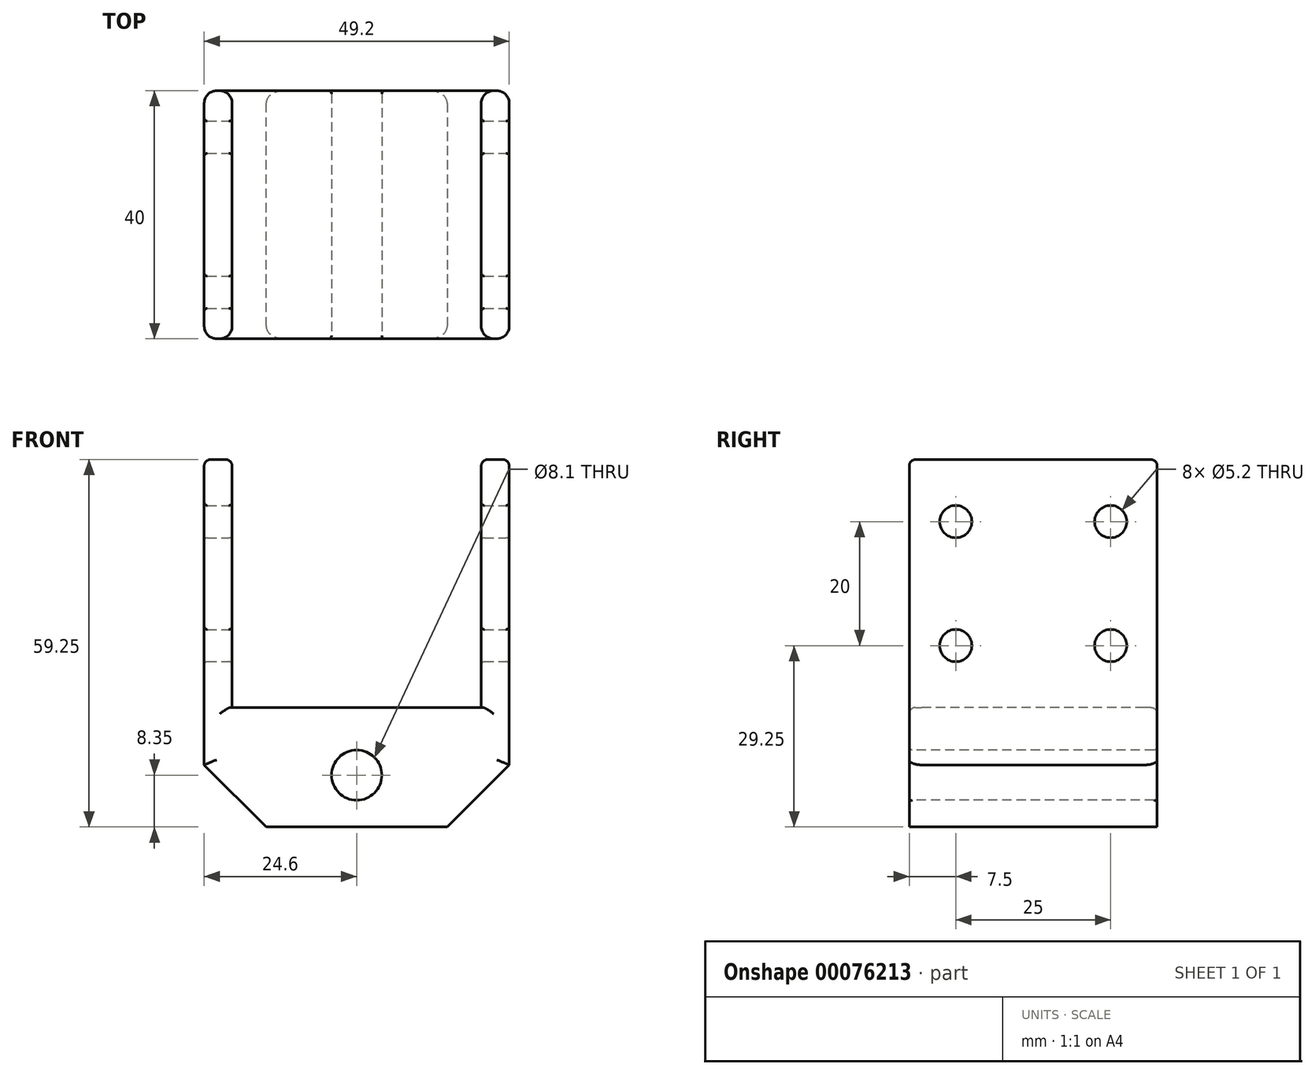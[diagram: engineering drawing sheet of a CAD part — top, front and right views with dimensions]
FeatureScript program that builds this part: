
annotation { "Feature Type Name" : "Feature", "Feature Type Description" : "" }
export const myFeature = defineFeature(function(context is Context, id is Id, definition is map)
    precondition{}
    {
        {
            assignVariable(context, id + "F0", {"name" : "HolderW", "anyValue" : 4.5});
        }
        {
            assignVariable(context, id + "F1", {"name" : "PlateH", "anyValue" : 6.75});
        }
        {
            assignVariable(context, id + "F2", {"name" : "RodD", "anyValue" : 8});
        }
        {
            assignVariable(context, id + "F3", {"name" : "ExtrusionH", "anyValue" : 40});
        }
        {
            var Q0;
            Q0=qCreatedBy(makeId("Top.planeOp"),FACE);
            var sketch = newSketch(context, id + "F4", { "sketchPlane" : qUnion([Q0])});
            skLineSegment(sketch, "E0.bottom", {"start": v(-24.6, 20) * mm, "end": v(24.6, 20) * mm});
            skLineSegment(sketch, "E0.top", {"start": v(-24.6, -20) * mm, "end": v(24.6, -20) * mm});
            skLineSegment(sketch, "E0.left", {"start": v(-24.6, 20) * mm, "end": v(-24.6, -20) * mm});
            skLineSegment(sketch, "E0.right", {"start": v(24.6, 20) * mm, "end": v(24.6, -20) * mm});
            skLineSegment(sketch, "E1", {"start": v(-20.1, 20) * mm, "end": v(-20.1, -20) * mm, "construction": true});
            skLineSegment(sketch, "E2", {"start": v(20.1, 20) * mm, "end": v(20.1, -20) * mm, "construction": true});
            skSolve(sketch);
        }
        {
            var Q0;
            Q0 = qSketchRegion(id + "F4", true);
            extrude(context, id + "F5", {"entities" : qUnion([Q0]), "depth" : (getVariable(context, 'HolderW') + getVariable(context, 'RodD') + getVariable(context, 'PlateH')) * mm});
        }
        {
            var Q0;
            Q0=makeQuery(id+"F5.opExtrude","CAP_FACE",FACE,{"disambiguationData":[OSD([sQuery(id+"F4.wireOp",EDGE,"E0.bottom"),sQuery(id+"F4.wireOp",EDGE,"E0.top"),sQuery(id+"F4.wireOp",EDGE,"E0.left"),sQuery(id+"F4.wireOp",EDGE,"E0.right")])],"isStart":false});
            var sketch = newSketch(context, id + "F6", { "sketchPlane" : qUnion([Q0])});
            skLineSegment(sketch, "E3", {"start": v(-20.1, 20) * mm, "end": v(-20.1, -20) * mm});
            skLineSegment(sketch, "E4", {"start": v(20.1, 20) * mm, "end": v(20.1, -20) * mm});
            skSolve(sketch);
        }
        {
            var Q0;
            {var subQ0=sQuery(id+"F6.wireOp",EDGE,"E3");Q0=makeQuery(id+"F6.imprint","IMPRINT",FACE,{"disambiguationData":[TD([[makeQuery(id+"F6.imprint","IMPRINT",EDGE,{"derivedFrom":subQ0}),-1.0]])]});}
            var Q1;
            {var subQ0=sQuery(id+"F6.wireOp",EDGE,"E4");Q1=makeQuery(id+"F6.imprint","IMPRINT",FACE,{"disambiguationData":[TD([[makeQuery(id+"F6.imprint","IMPRINT",EDGE,{"derivedFrom":subQ0}),1.0]])]});}
            extrude(context, id + "F7", {"entities" : qUnion([Q0, Q1]), "operationType" : NewBodyOperationType.ADD, "depth" : (getVariable(context, 'ExtrusionH')) * mm});
        }
        {
            var Q0;
            {var subQ0=sQuery(id+"F4.wireOp",EDGE,"E0.top");var subQ1=makeQuery(id+"F5.opExtrude","CAP_EDGE",EDGE,{"disambiguationData":[OSD([subQ0])],"isStart":false});Q0=makeQuery(id+"F7.boolean.opBoolean","MERGE",FACE,{"derivedFrom":[makeQuery(id+"F5.opExtrude","SWEPT_FACE",FACE,{"disambiguationData":[OSD([subQ0])]}),makeQuery(id+"F7.opExtrude","SWEPT_FACE",FACE,{"disambiguationData":[OSD([subQ0]),TDD([makeQuery(id+"F6.imprint","IMPRINT",EDGE,{"disambiguationData":[TD([[makeQuery(id+"F6.imprint","INTERSECT",VERTEX,{"derivedFrom":[subQ1,makeQuery(id+"F5.opExtrude","CAP_EDGE",EDGE,{"disambiguationData":[OSD([sQuery(id+"F4.wireOp",EDGE,"E0.left")])],"isStart":false})]}),-1.0]])],"derivedFrom":subQ1})])]}),makeQuery(id+"F7.opExtrude","SWEPT_FACE",FACE,{"disambiguationData":[OSD([subQ0]),TDD([makeQuery(id+"F6.imprint","IMPRINT",EDGE,{"disambiguationData":[TD([[makeQuery(id+"F6.imprint","INTERSECT",VERTEX,{"derivedFrom":[subQ1,makeQuery(id+"F5.opExtrude","CAP_EDGE",EDGE,{"disambiguationData":[OSD([sQuery(id+"F4.wireOp",EDGE,"E0.right")])],"isStart":false})]}),1.0]])],"derivedFrom":subQ1})])]})]});}
            var sketch = newSketch(context, id + "F8", { "sketchPlane" : qUnion([Q0])});
            skCircle(sketch, "E5", {"center": v(0, 8.35) * mm, "radius": 4.05 * mm});
            skSolve(sketch);
        }
        {
            var Q0;
            Q0=makeQuery(id+"F8.imprint","IMPRINT",FACE,{"disambiguationData":[TD([[makeQuery(id+"F8.imprint","IMPRINT",EDGE,{"derivedFrom":sQuery(id+"F8.wireOp",EDGE,"E5")}),1.0]])]});
            var Q1;
            {var subQ0=sQuery(id+"F4.wireOp",EDGE,"E0.bottom");var subQ1=makeQuery(id+"F5.opExtrude","CAP_EDGE",EDGE,{"disambiguationData":[OSD([subQ0])],"isStart":false});Q1=makeQuery(id+"F7.boolean.opBoolean","MERGE",FACE,{"derivedFrom":[makeQuery(id+"F5.opExtrude","SWEPT_FACE",FACE,{"disambiguationData":[OSD([subQ0])]}),makeQuery(id+"F7.opExtrude","SWEPT_FACE",FACE,{"disambiguationData":[OSD([subQ0]),TDD([makeQuery(id+"F6.imprint","IMPRINT",EDGE,{"disambiguationData":[TD([[makeQuery(id+"F6.imprint","INTERSECT",VERTEX,{"derivedFrom":[subQ1,makeQuery(id+"F5.opExtrude","CAP_EDGE",EDGE,{"disambiguationData":[OSD([sQuery(id+"F4.wireOp",EDGE,"E0.left")])],"isStart":false})]}),-1.0]])],"derivedFrom":subQ1})])]}),makeQuery(id+"F7.opExtrude","SWEPT_FACE",FACE,{"disambiguationData":[OSD([subQ0]),TDD([makeQuery(id+"F6.imprint","IMPRINT",EDGE,{"disambiguationData":[TD([[makeQuery(id+"F6.imprint","INTERSECT",VERTEX,{"derivedFrom":[subQ1,makeQuery(id+"F5.opExtrude","CAP_EDGE",EDGE,{"disambiguationData":[OSD([sQuery(id+"F4.wireOp",EDGE,"E0.right")])],"isStart":false})]}),1.0]])],"derivedFrom":subQ1})])]})]});}
            extrude(context, id + "F9", {"entities" : qUnion([Q0]), "operationType" : NewBodyOperationType.REMOVE, "endBound" : BoundingType.UP_TO_SURFACE, "oppositeDirection" : true, "endBoundEntityFace" : qUnion([Q1]), "depth" : 25 * mm});
        }
        {
            var Q0;
            Q0=makeQuery(id+"F5.opExtrude","CAP_EDGE",EDGE,{"disambiguationData":[OSD([sQuery(id+"F4.wireOp",EDGE,"E0.left")])],"isStart":true});
            var Q1;
            Q1=makeQuery(id+"F5.opExtrude","CAP_EDGE",EDGE,{"disambiguationData":[OSD([sQuery(id+"F4.wireOp",EDGE,"E0.right")])],"isStart":true});
            chamfer(context, id + "F10", {"entities" : qUnion([Q0, Q1]), "width" : 10 * mm, "tangentPropagation" : true});
        }
        {
            var Q0;
            {var subQ0=sQuery(id+"F4.wireOp",EDGE,"E0.right");Q0=makeQuery(id+"F7.boolean.opBoolean","MERGE",FACE,{"derivedFrom":[makeQuery(id+"F5.opExtrude","SWEPT_FACE",FACE,{"disambiguationData":[OSD([subQ0])]}),makeQuery(id+"F7.opExtrude","SWEPT_FACE",FACE,{"disambiguationData":[OSD([subQ0])]})]});}
            var sketch = newSketch(context, id + "F11", { "sketchPlane" : qUnion([Q0])});
            skCircle(sketch, "E6", {"center": v(-12.5, 49.25) * mm, "radius": 2.6 * mm});
            skCircle(sketch, "E7", {"center": v(-12.5, 29.25) * mm, "radius": 2.6 * mm});
            skCircle(sketch, "E8", {"center": v(12.5, 49.25) * mm, "radius": 2.6 * mm});
            skCircle(sketch, "E9", {"center": v(12.5, 29.25) * mm, "radius": 2.6 * mm});
            skLineSegment(sketch, "E10.bottom", {"start": v(-12.5, 49.25) * mm, "end": v(12.5, 49.25) * mm, "construction": true});
            skLineSegment(sketch, "E10.top", {"start": v(-12.5, 29.25) * mm, "end": v(12.5, 29.25) * mm, "construction": true});
            skLineSegment(sketch, "E10.left", {"start": v(-12.5, 49.25) * mm, "end": v(-12.5, 29.25) * mm, "construction": true});
            skLineSegment(sketch, "E10.right", {"start": v(12.5, 49.25) * mm, "end": v(12.5, 29.25) * mm, "construction": true});
            skSolve(sketch);
        }
        {
            var Q0;
            Q0 = qSketchRegion(id + "F11", true);
            var Q1;
            {var subQ0=sQuery(id+"F4.wireOp",EDGE,"E0.left");Q1=makeQuery(id+"F7.boolean.opBoolean","MERGE",FACE,{"derivedFrom":[makeQuery(id+"F5.opExtrude","SWEPT_FACE",FACE,{"disambiguationData":[OSD([subQ0])]}),makeQuery(id+"F7.opExtrude","SWEPT_FACE",FACE,{"disambiguationData":[OSD([subQ0])]})]});}
            extrude(context, id + "F12", {"entities" : qUnion([Q0]), "operationType" : NewBodyOperationType.REMOVE, "endBound" : BoundingType.UP_TO_SURFACE, "oppositeDirection" : true, "endBoundEntityFace" : qUnion([Q1]), "depth" : 25 * mm});
        }
        {
            var Q0;
            Q0=makeQuery(id+"F7.opExtrude","SWEPT_EDGE",EDGE,{"disambiguationData":[OSD([sQuery(id+"F4.wireOp",EDGE,"E0.top"),sQuery(id+"F6.wireOp",EDGE,"E3")])]});
            var Q1;
            {var subQ0=sQuery(id+"F4.wireOp",EDGE,"E0.left");var subQ1=sQuery(id+"F4.wireOp",EDGE,"E0.top");Q1=makeQuery(id+"F7.boolean.opBoolean","MERGE",EDGE,{"derivedFrom":[makeQuery(id+"F5.opExtrude","SWEPT_EDGE",EDGE,{"disambiguationData":[OSD([subQ1,subQ0])]}),makeQuery(id+"F7.opExtrude","SWEPT_EDGE",EDGE,{"disambiguationData":[OSD([subQ1,subQ0])]})]});}
            var Q2;
            Q2=makeQuery(id+"F7.opExtrude","SWEPT_EDGE",EDGE,{"disambiguationData":[OSD([sQuery(id+"F4.wireOp",EDGE,"E0.top"),sQuery(id+"F6.wireOp",EDGE,"E4")])]});
            var Q3;
            {var subQ0=sQuery(id+"F4.wireOp",EDGE,"E0.right");var subQ1=sQuery(id+"F4.wireOp",EDGE,"E0.top");Q3=makeQuery(id+"F7.boolean.opBoolean","MERGE",EDGE,{"derivedFrom":[makeQuery(id+"F5.opExtrude","SWEPT_EDGE",EDGE,{"disambiguationData":[OSD([subQ1,subQ0])]}),makeQuery(id+"F7.opExtrude","SWEPT_EDGE",EDGE,{"disambiguationData":[OSD([subQ1,subQ0])]})]});}
            var Q4;
            {var subQ0=sQuery(id+"F4.wireOp",EDGE,"E0.top");var subQ1=makeQuery(id+"F5.opExtrude","CAP_EDGE",EDGE,{"disambiguationData":[OSD([subQ0])],"isStart":false});var subQ2=sQuery(id+"F4.wireOp",EDGE,"E0.left");Q4=makeQuery(id+"F10.opChamfer","BLEND_EDGE",EDGE,{"blendedFrom":[makeQuery(id+"F5.opExtrude","CAP_EDGE",EDGE,{"disambiguationData":[OSD([subQ2])],"isStart":true}),makeQuery(id+"F7.boolean.opBoolean","MERGE",FACE,{"derivedFrom":[makeQuery(id+"F5.opExtrude","SWEPT_FACE",FACE,{"disambiguationData":[OSD([subQ0])]}),makeQuery(id+"F7.opExtrude","SWEPT_FACE",FACE,{"disambiguationData":[OSD([subQ0]),TDD([makeQuery(id+"F6.imprint","IMPRINT",EDGE,{"disambiguationData":[TD([[makeQuery(id+"F6.imprint","INTERSECT",VERTEX,{"derivedFrom":[subQ1,makeQuery(id+"F5.opExtrude","CAP_EDGE",EDGE,{"disambiguationData":[OSD([subQ2])],"isStart":false})]}),-1.0]])],"derivedFrom":subQ1})])]}),makeQuery(id+"F7.opExtrude","SWEPT_FACE",FACE,{"disambiguationData":[OSD([subQ0]),TDD([makeQuery(id+"F6.imprint","IMPRINT",EDGE,{"disambiguationData":[TD([[makeQuery(id+"F6.imprint","INTERSECT",VERTEX,{"derivedFrom":[subQ1,makeQuery(id+"F5.opExtrude","CAP_EDGE",EDGE,{"disambiguationData":[OSD([sQuery(id+"F4.wireOp",EDGE,"E0.right")])],"isStart":false})]}),1.0]])],"derivedFrom":subQ1})])]})]})],"blendedInto":[makeQuery(id+"F7.boolean.opBoolean","MERGE",FACE,{"derivedFrom":[makeQuery(id+"F5.opExtrude","SWEPT_FACE",FACE,{"disambiguationData":[OSD([subQ0])]}),makeQuery(id+"F7.opExtrude","SWEPT_FACE",FACE,{"disambiguationData":[OSD([subQ0]),TDD([makeQuery(id+"F6.imprint","IMPRINT",EDGE,{"disambiguationData":[TD([[makeQuery(id+"F6.imprint","INTERSECT",VERTEX,{"derivedFrom":[subQ1,makeQuery(id+"F5.opExtrude","CAP_EDGE",EDGE,{"disambiguationData":[OSD([subQ2])],"isStart":false})]}),-1.0]])],"derivedFrom":subQ1})])]}),makeQuery(id+"F7.opExtrude","SWEPT_FACE",FACE,{"disambiguationData":[OSD([subQ0]),TDD([makeQuery(id+"F6.imprint","IMPRINT",EDGE,{"disambiguationData":[TD([[makeQuery(id+"F6.imprint","INTERSECT",VERTEX,{"derivedFrom":[subQ1,makeQuery(id+"F5.opExtrude","CAP_EDGE",EDGE,{"disambiguationData":[OSD([sQuery(id+"F4.wireOp",EDGE,"E0.right")])],"isStart":false})]}),1.0]])],"derivedFrom":subQ1})])]})]})]});}
            var Q5;
            {var subQ0=sQuery(id+"F4.wireOp",EDGE,"E0.right");var subQ1=sQuery(id+"F4.wireOp",EDGE,"E0.top");var subQ2=makeQuery(id+"F5.opExtrude","CAP_EDGE",EDGE,{"disambiguationData":[OSD([subQ1])],"isStart":false});Q5=makeQuery(id+"F10.opChamfer","BLEND_EDGE",EDGE,{"blendedFrom":[makeQuery(id+"F5.opExtrude","CAP_EDGE",EDGE,{"disambiguationData":[OSD([subQ0])],"isStart":true}),makeQuery(id+"F7.boolean.opBoolean","MERGE",FACE,{"derivedFrom":[makeQuery(id+"F5.opExtrude","SWEPT_FACE",FACE,{"disambiguationData":[OSD([subQ1])]}),makeQuery(id+"F7.opExtrude","SWEPT_FACE",FACE,{"disambiguationData":[OSD([subQ1]),TDD([makeQuery(id+"F6.imprint","IMPRINT",EDGE,{"disambiguationData":[TD([[makeQuery(id+"F6.imprint","INTERSECT",VERTEX,{"derivedFrom":[subQ2,makeQuery(id+"F5.opExtrude","CAP_EDGE",EDGE,{"disambiguationData":[OSD([sQuery(id+"F4.wireOp",EDGE,"E0.left")])],"isStart":false})]}),-1.0]])],"derivedFrom":subQ2})])]}),makeQuery(id+"F7.opExtrude","SWEPT_FACE",FACE,{"disambiguationData":[OSD([subQ1]),TDD([makeQuery(id+"F6.imprint","IMPRINT",EDGE,{"disambiguationData":[TD([[makeQuery(id+"F6.imprint","INTERSECT",VERTEX,{"derivedFrom":[subQ2,makeQuery(id+"F5.opExtrude","CAP_EDGE",EDGE,{"disambiguationData":[OSD([subQ0])],"isStart":false})]}),1.0]])],"derivedFrom":subQ2})])]})]})],"blendedInto":[makeQuery(id+"F7.boolean.opBoolean","MERGE",FACE,{"derivedFrom":[makeQuery(id+"F5.opExtrude","SWEPT_FACE",FACE,{"disambiguationData":[OSD([subQ1])]}),makeQuery(id+"F7.opExtrude","SWEPT_FACE",FACE,{"disambiguationData":[OSD([subQ1]),TDD([makeQuery(id+"F6.imprint","IMPRINT",EDGE,{"disambiguationData":[TD([[makeQuery(id+"F6.imprint","INTERSECT",VERTEX,{"derivedFrom":[subQ2,makeQuery(id+"F5.opExtrude","CAP_EDGE",EDGE,{"disambiguationData":[OSD([sQuery(id+"F4.wireOp",EDGE,"E0.left")])],"isStart":false})]}),-1.0]])],"derivedFrom":subQ2})])]}),makeQuery(id+"F7.opExtrude","SWEPT_FACE",FACE,{"disambiguationData":[OSD([subQ1]),TDD([makeQuery(id+"F6.imprint","IMPRINT",EDGE,{"disambiguationData":[TD([[makeQuery(id+"F6.imprint","INTERSECT",VERTEX,{"derivedFrom":[subQ2,makeQuery(id+"F5.opExtrude","CAP_EDGE",EDGE,{"disambiguationData":[OSD([subQ0])],"isStart":false})]}),1.0]])],"derivedFrom":subQ2})])]})]})]});}
            var Q6;
            {var subQ0=sQuery(id+"F4.wireOp",EDGE,"E0.right");var subQ1=sQuery(id+"F4.wireOp",EDGE,"E0.bottom");Q6=makeQuery(id+"F7.boolean.opBoolean","MERGE",EDGE,{"derivedFrom":[makeQuery(id+"F5.opExtrude","SWEPT_EDGE",EDGE,{"disambiguationData":[OSD([subQ1,subQ0])]}),makeQuery(id+"F7.opExtrude","SWEPT_EDGE",EDGE,{"disambiguationData":[OSD([subQ1,subQ0])]})]});}
            var Q7;
            Q7=makeQuery(id+"F7.opExtrude","SWEPT_EDGE",EDGE,{"disambiguationData":[OSD([sQuery(id+"F4.wireOp",EDGE,"E0.bottom"),sQuery(id+"F6.wireOp",EDGE,"E4")])]});
            var Q8;
            {var subQ0=sQuery(id+"F4.wireOp",EDGE,"E0.right");var subQ1=sQuery(id+"F4.wireOp",EDGE,"E0.bottom");var subQ2=makeQuery(id+"F5.opExtrude","CAP_EDGE",EDGE,{"disambiguationData":[OSD([subQ1])],"isStart":false});Q8=makeQuery(id+"F10.opChamfer","BLEND_EDGE",EDGE,{"blendedFrom":[makeQuery(id+"F5.opExtrude","CAP_EDGE",EDGE,{"disambiguationData":[OSD([subQ0])],"isStart":true}),makeQuery(id+"F7.boolean.opBoolean","MERGE",FACE,{"derivedFrom":[makeQuery(id+"F5.opExtrude","SWEPT_FACE",FACE,{"disambiguationData":[OSD([subQ1])]}),makeQuery(id+"F7.opExtrude","SWEPT_FACE",FACE,{"disambiguationData":[OSD([subQ1]),TDD([makeQuery(id+"F6.imprint","IMPRINT",EDGE,{"disambiguationData":[TD([[makeQuery(id+"F6.imprint","INTERSECT",VERTEX,{"derivedFrom":[subQ2,makeQuery(id+"F5.opExtrude","CAP_EDGE",EDGE,{"disambiguationData":[OSD([sQuery(id+"F4.wireOp",EDGE,"E0.left")])],"isStart":false})]}),-1.0]])],"derivedFrom":subQ2})])]}),makeQuery(id+"F7.opExtrude","SWEPT_FACE",FACE,{"disambiguationData":[OSD([subQ1]),TDD([makeQuery(id+"F6.imprint","IMPRINT",EDGE,{"disambiguationData":[TD([[makeQuery(id+"F6.imprint","INTERSECT",VERTEX,{"derivedFrom":[subQ2,makeQuery(id+"F5.opExtrude","CAP_EDGE",EDGE,{"disambiguationData":[OSD([subQ0])],"isStart":false})]}),1.0]])],"derivedFrom":subQ2})])]})]})],"blendedInto":[makeQuery(id+"F7.boolean.opBoolean","MERGE",FACE,{"derivedFrom":[makeQuery(id+"F5.opExtrude","SWEPT_FACE",FACE,{"disambiguationData":[OSD([subQ1])]}),makeQuery(id+"F7.opExtrude","SWEPT_FACE",FACE,{"disambiguationData":[OSD([subQ1]),TDD([makeQuery(id+"F6.imprint","IMPRINT",EDGE,{"disambiguationData":[TD([[makeQuery(id+"F6.imprint","INTERSECT",VERTEX,{"derivedFrom":[subQ2,makeQuery(id+"F5.opExtrude","CAP_EDGE",EDGE,{"disambiguationData":[OSD([sQuery(id+"F4.wireOp",EDGE,"E0.left")])],"isStart":false})]}),-1.0]])],"derivedFrom":subQ2})])]}),makeQuery(id+"F7.opExtrude","SWEPT_FACE",FACE,{"disambiguationData":[OSD([subQ1]),TDD([makeQuery(id+"F6.imprint","IMPRINT",EDGE,{"disambiguationData":[TD([[makeQuery(id+"F6.imprint","INTERSECT",VERTEX,{"derivedFrom":[subQ2,makeQuery(id+"F5.opExtrude","CAP_EDGE",EDGE,{"disambiguationData":[OSD([subQ0])],"isStart":false})]}),1.0]])],"derivedFrom":subQ2})])]})]})]});}
            var Q9;
            Q9=makeQuery(id+"F7.opExtrude","SWEPT_EDGE",EDGE,{"disambiguationData":[OSD([sQuery(id+"F4.wireOp",EDGE,"E0.bottom"),sQuery(id+"F6.wireOp",EDGE,"E3")])]});
            var Q10;
            {var subQ0=sQuery(id+"F4.wireOp",EDGE,"E0.left");var subQ1=sQuery(id+"F4.wireOp",EDGE,"E0.bottom");Q10=makeQuery(id+"F7.boolean.opBoolean","MERGE",EDGE,{"derivedFrom":[makeQuery(id+"F5.opExtrude","SWEPT_EDGE",EDGE,{"disambiguationData":[OSD([subQ1,subQ0])]}),makeQuery(id+"F7.opExtrude","SWEPT_EDGE",EDGE,{"disambiguationData":[OSD([subQ1,subQ0])]})]});}
            var Q11;
            {var subQ0=sQuery(id+"F4.wireOp",EDGE,"E0.bottom");var subQ1=makeQuery(id+"F5.opExtrude","CAP_EDGE",EDGE,{"disambiguationData":[OSD([subQ0])],"isStart":false});var subQ2=sQuery(id+"F4.wireOp",EDGE,"E0.left");Q11=makeQuery(id+"F10.opChamfer","BLEND_EDGE",EDGE,{"blendedFrom":[makeQuery(id+"F5.opExtrude","CAP_EDGE",EDGE,{"disambiguationData":[OSD([subQ2])],"isStart":true}),makeQuery(id+"F7.boolean.opBoolean","MERGE",FACE,{"derivedFrom":[makeQuery(id+"F5.opExtrude","SWEPT_FACE",FACE,{"disambiguationData":[OSD([subQ0])]}),makeQuery(id+"F7.opExtrude","SWEPT_FACE",FACE,{"disambiguationData":[OSD([subQ0]),TDD([makeQuery(id+"F6.imprint","IMPRINT",EDGE,{"disambiguationData":[TD([[makeQuery(id+"F6.imprint","INTERSECT",VERTEX,{"derivedFrom":[subQ1,makeQuery(id+"F5.opExtrude","CAP_EDGE",EDGE,{"disambiguationData":[OSD([subQ2])],"isStart":false})]}),-1.0]])],"derivedFrom":subQ1})])]}),makeQuery(id+"F7.opExtrude","SWEPT_FACE",FACE,{"disambiguationData":[OSD([subQ0]),TDD([makeQuery(id+"F6.imprint","IMPRINT",EDGE,{"disambiguationData":[TD([[makeQuery(id+"F6.imprint","INTERSECT",VERTEX,{"derivedFrom":[subQ1,makeQuery(id+"F5.opExtrude","CAP_EDGE",EDGE,{"disambiguationData":[OSD([sQuery(id+"F4.wireOp",EDGE,"E0.right")])],"isStart":false})]}),1.0]])],"derivedFrom":subQ1})])]})]})],"blendedInto":[makeQuery(id+"F7.boolean.opBoolean","MERGE",FACE,{"derivedFrom":[makeQuery(id+"F5.opExtrude","SWEPT_FACE",FACE,{"disambiguationData":[OSD([subQ0])]}),makeQuery(id+"F7.opExtrude","SWEPT_FACE",FACE,{"disambiguationData":[OSD([subQ0]),TDD([makeQuery(id+"F6.imprint","IMPRINT",EDGE,{"disambiguationData":[TD([[makeQuery(id+"F6.imprint","INTERSECT",VERTEX,{"derivedFrom":[subQ1,makeQuery(id+"F5.opExtrude","CAP_EDGE",EDGE,{"disambiguationData":[OSD([subQ2])],"isStart":false})]}),-1.0]])],"derivedFrom":subQ1})])]}),makeQuery(id+"F7.opExtrude","SWEPT_FACE",FACE,{"disambiguationData":[OSD([subQ0]),TDD([makeQuery(id+"F6.imprint","IMPRINT",EDGE,{"disambiguationData":[TD([[makeQuery(id+"F6.imprint","INTERSECT",VERTEX,{"derivedFrom":[subQ1,makeQuery(id+"F5.opExtrude","CAP_EDGE",EDGE,{"disambiguationData":[OSD([sQuery(id+"F4.wireOp",EDGE,"E0.right")])],"isStart":false})]}),1.0]])],"derivedFrom":subQ1})])]})]})]});}
            fillet(context, id + "F13", {"entities" : qUnion([Q0, Q1, Q2, Q3, Q4, Q5, Q6, Q7, Q8, Q9, Q10, Q11]), "radius" : 2 * mm, "tangentPropagation" : true, "allowEdgeOverflow" : false});
        }
        {
            var Q0;
            Q0=makeQuery(id+"F9.boolean.opBoolean","COPY",FACE,{"derivedFrom":makeQuery(id+"F9.opExtrude","SWEPT_FACE",FACE,{"disambiguationData":[OSD([sQuery(id+"F8.wireOp",EDGE,"E5")])]})});
            var Q1;
            Q1=makeQuery(id+"F12.boolean.opBoolean","COPY",FACE,{"disambiguationData":[OD(1.0)],"derivedFrom":makeQuery(id+"F12.opExtrude","SWEPT_FACE",FACE,{"disambiguationData":[OSD([sQuery(id+"F11.wireOp",EDGE,"E9")])]})});
            var Q2;
            Q2=makeQuery(id+"F12.boolean.opBoolean","COPY",FACE,{"disambiguationData":[OD(1.0)],"derivedFrom":makeQuery(id+"F12.opExtrude","SWEPT_FACE",FACE,{"disambiguationData":[OSD([sQuery(id+"F11.wireOp",EDGE,"E8")])]})});
            var Q3;
            Q3=makeQuery(id+"F12.boolean.opBoolean","COPY",FACE,{"disambiguationData":[OD(1.0)],"derivedFrom":makeQuery(id+"F12.opExtrude","SWEPT_FACE",FACE,{"disambiguationData":[OSD([sQuery(id+"F11.wireOp",EDGE,"E6")])]})});
            var Q4;
            Q4=makeQuery(id+"F12.boolean.opBoolean","COPY",FACE,{"disambiguationData":[OD(1.0)],"derivedFrom":makeQuery(id+"F12.opExtrude","SWEPT_FACE",FACE,{"disambiguationData":[OSD([sQuery(id+"F11.wireOp",EDGE,"E7")])]})});
            var Q5;
            Q5=makeQuery(id+"F12.boolean.opBoolean","COPY",FACE,{"disambiguationData":[OD(0.0)],"derivedFrom":makeQuery(id+"F12.opExtrude","SWEPT_FACE",FACE,{"disambiguationData":[OSD([sQuery(id+"F11.wireOp",EDGE,"E7")])]})});
            var Q6;
            Q6=makeQuery(id+"F12.boolean.opBoolean","COPY",FACE,{"disambiguationData":[OD(0.0)],"derivedFrom":makeQuery(id+"F12.opExtrude","SWEPT_FACE",FACE,{"disambiguationData":[OSD([sQuery(id+"F11.wireOp",EDGE,"E6")])]})});
            var Q7;
            Q7=makeQuery(id+"F12.boolean.opBoolean","COPY",FACE,{"disambiguationData":[OD(0.0)],"derivedFrom":makeQuery(id+"F12.opExtrude","SWEPT_FACE",FACE,{"disambiguationData":[OSD([sQuery(id+"F11.wireOp",EDGE,"E8")])]})});
            var Q8;
            Q8=makeQuery(id+"F12.boolean.opBoolean","COPY",FACE,{"disambiguationData":[OD(0.0)],"derivedFrom":makeQuery(id+"F12.opExtrude","SWEPT_FACE",FACE,{"disambiguationData":[OSD([sQuery(id+"F11.wireOp",EDGE,"E9")])]})});
            fillet(context, id + "F14", {"entities" : qUnion([Q0, Q1, Q2, Q3, Q4, Q5, Q6, Q7, Q8]), "radius" : 0.5 * mm, "tangentPropagation" : true, "allowEdgeOverflow" : false});
        }
        {
            var Q0;
            Q0=makeQuery(id+"F7.opExtrude","CAP_FACE",FACE,{"disambiguationData":[OSD([sQuery(id+"F4.wireOp",EDGE,"E0.bottom"),sQuery(id+"F4.wireOp",EDGE,"E0.top"),sQuery(id+"F4.wireOp",EDGE,"E0.right"),sQuery(id+"F6.wireOp",EDGE,"E4")])],"isStart":false});
            var Q1;
            Q1=makeQuery(id+"F7.opExtrude","CAP_FACE",FACE,{"disambiguationData":[OSD([sQuery(id+"F4.wireOp",EDGE,"E0.bottom"),sQuery(id+"F4.wireOp",EDGE,"E0.top"),sQuery(id+"F4.wireOp",EDGE,"E0.left"),sQuery(id+"F6.wireOp",EDGE,"E3")])],"isStart":false});
            var Q2;
            Q2=makeQuery(id+"F5.opExtrude","CAP_EDGE",EDGE,{"disambiguationData":[OSD([sQuery(id+"F4.wireOp",EDGE,"E0.bottom")])],"isStart":false});
            var Q3;
            Q3=makeQuery(id+"F5.opExtrude","CAP_EDGE",EDGE,{"disambiguationData":[OSD([sQuery(id+"F4.wireOp",EDGE,"E0.top")])],"isStart":false});
            fillet(context, id + "F15", {"entities" : qUnion([Q0, Q1, Q2, Q3]), "radius" : 1 * mm, "tangentPropagation" : true, "allowEdgeOverflow" : false});
        }
    });
